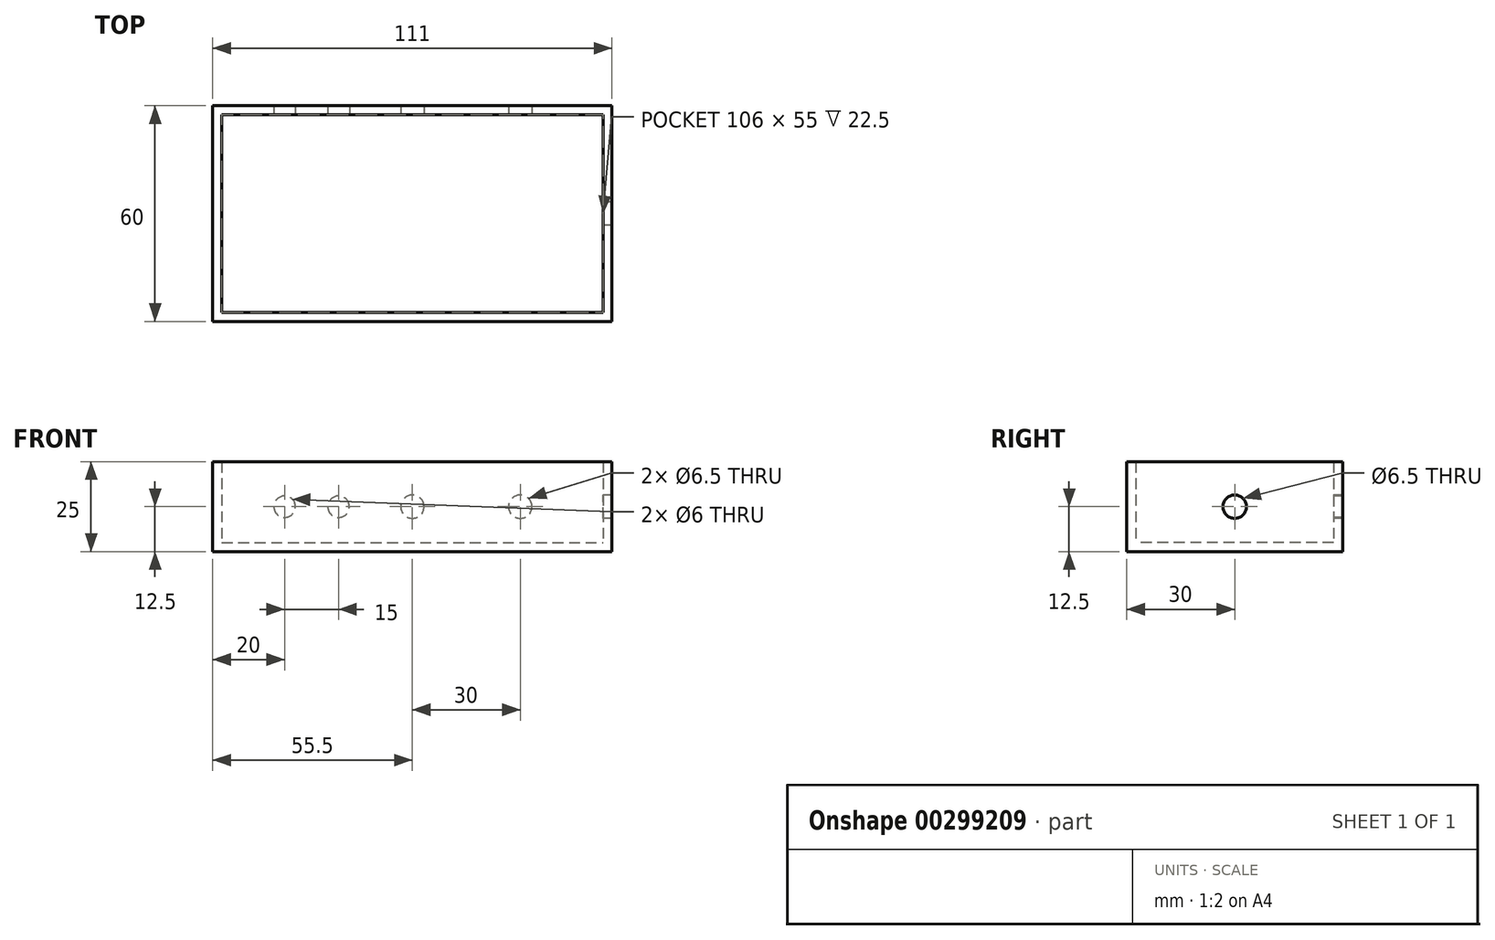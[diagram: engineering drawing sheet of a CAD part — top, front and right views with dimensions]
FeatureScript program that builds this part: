
annotation { "Feature Type Name" : "Feature", "Feature Type Description" : "" }
export const myFeature = defineFeature(function(context is Context, id is Id, definition is map)
    precondition{}
    {
        {
            var Q0;
            Q0=qCreatedBy(makeId("Top.planeOp"),FACE);
            var sketch = newSketch(context, id + "F0", { "sketchPlane" : qUnion([Q0])});
            skLineSegment(sketch, "E0.bottom", {"start": v(-55.5, 30) * mm, "end": v(55.5, 30) * mm});
            skLineSegment(sketch, "E0.top", {"start": v(-55.5, -30) * mm, "end": v(55.5, -30) * mm});
            skLineSegment(sketch, "E0.left", {"start": v(-55.5, 30) * mm, "end": v(-55.5, -30) * mm});
            skLineSegment(sketch, "E0.right", {"start": v(55.5, 30) * mm, "end": v(55.5, -30) * mm});
            skPoint(sketch, "E0.middle", {"position": v(0, 0) * mm});
            skSolve(sketch);
        }
        {
            var Q0;
            Q0=qSketchRegion(id+"F0",true);
            extrude(context, id + "F1", {"entities" : qUnion([Q0]), "depth" : 25 * mm, "offsetDistance" : 25 * mm});
        }
        {
            var Q0;
            Q0=makeQuery(id+"F1.opExtrude","CAP_FACE",FACE,{"disambiguationData":[OSD([sQuery(id+"F0.wireOp",EDGE,"E0.bottom"),sQuery(id+"F0.wireOp",EDGE,"E0.top"),sQuery(id+"F0.wireOp",EDGE,"E0.left"),sQuery(id+"F0.wireOp",EDGE,"E0.right")])],"isStart":false});
            shell(context, id + "F2", {"entities" : qUnion([Q0]), "thickness" : 2.5 * mm});
        }
        {
            var Q0;
            Q0=qCreatedBy(makeId("Right.planeOp"),FACE);
            var sketch = newSketch(context, id + "F3", { "sketchPlane" : qUnion([Q0])});
            skCircle(sketch, "E1", {"center": v(0, 12.5) * mm, "radius": 3.25 * mm});
            skSolve(sketch);
        }
        {
            var Q0;
            Q0=qSketchRegion(id+"F3",true);
            var Q1;
            Q1=makeQuery(id+"F1.opExtrude","SWEPT_FACE",FACE,{"disambiguationData":[OSD([sQuery(id+"F0.wireOp",EDGE,"E0.right")])]});
            extrude(context, id + "F4", {"entities" : qUnion([Q0]), "operationType" : NewBodyOperationType.REMOVE, "endBound" : BoundingType.UP_TO_SURFACE, "depth" : 25 * mm, "endBoundEntityFace" : qUnion([Q1]), "offsetDistance" : 25 * mm});
        }
        {
            var Q0;
            Q0=qCreatedBy(makeId("Front.planeOp"),FACE);
            var sketch = newSketch(context, id + "F5", { "sketchPlane" : qUnion([Q0])});
            skCircle(sketch, "E2", {"center": v(0, 12.5) * mm, "radius": 3.25 * mm});
            skCircle(sketch, "E3", {"center": v(30, 12.5) * mm, "radius": 3.25 * mm});
            skSolve(sketch);
        }
        {
            var Q0;
            Q0=qSketchRegion(id+"F5",true);
            var Q1;
            Q1=makeQuery(id+"F1.opExtrude","SWEPT_FACE",FACE,{"disambiguationData":[OSD([sQuery(id+"F0.wireOp",EDGE,"E0.bottom")])]});
            var Q2;
            Q2=makeQuery(id+"F1.opExtrude","SWEPT_FACE",FACE,{"disambiguationData":[OSD([sQuery(id+"F0.wireOp",EDGE,"E0.top")])]});
            extrude(context, id + "F6", {"entities" : qUnion([Q0]), "operationType" : NewBodyOperationType.REMOVE, "endBound" : BoundingType.UP_TO_SURFACE, "oppositeDirection" : true, "depth" : 25 * mm, "endBoundEntityFace" : qUnion([Q1]), "offsetDistance" : 25 * mm});
        }
        {
            var Q0;
            Q0=qCreatedBy(makeId("Front.planeOp"),FACE);
            var sketch = newSketch(context, id + "F7", { "sketchPlane" : qUnion([Q0])});
            skCircle(sketch, "E4", {"center": v(-35.5, 12.5) * mm, "radius": 3 * mm});
            skCircle(sketch, "E5", {"center": v(-20.5, 12.5) * mm, "radius": 3 * mm});
            skSolve(sketch);
        }
        {
            var Q0;
            Q0=qSketchRegion(id+"F7",true);
            var Q1;
            Q1=makeQuery(id+"F1.opExtrude","SWEPT_FACE",FACE,{"disambiguationData":[OSD([sQuery(id+"F0.wireOp",EDGE,"E0.bottom")])]});
            extrude(context, id + "F8", {"entities" : qUnion([Q0]), "operationType" : NewBodyOperationType.REMOVE, "endBound" : BoundingType.UP_TO_SURFACE, "oppositeDirection" : true, "depth" : 25 * mm, "endBoundEntityFace" : qUnion([Q1]), "offsetDistance" : 25 * mm});
        }
    });
